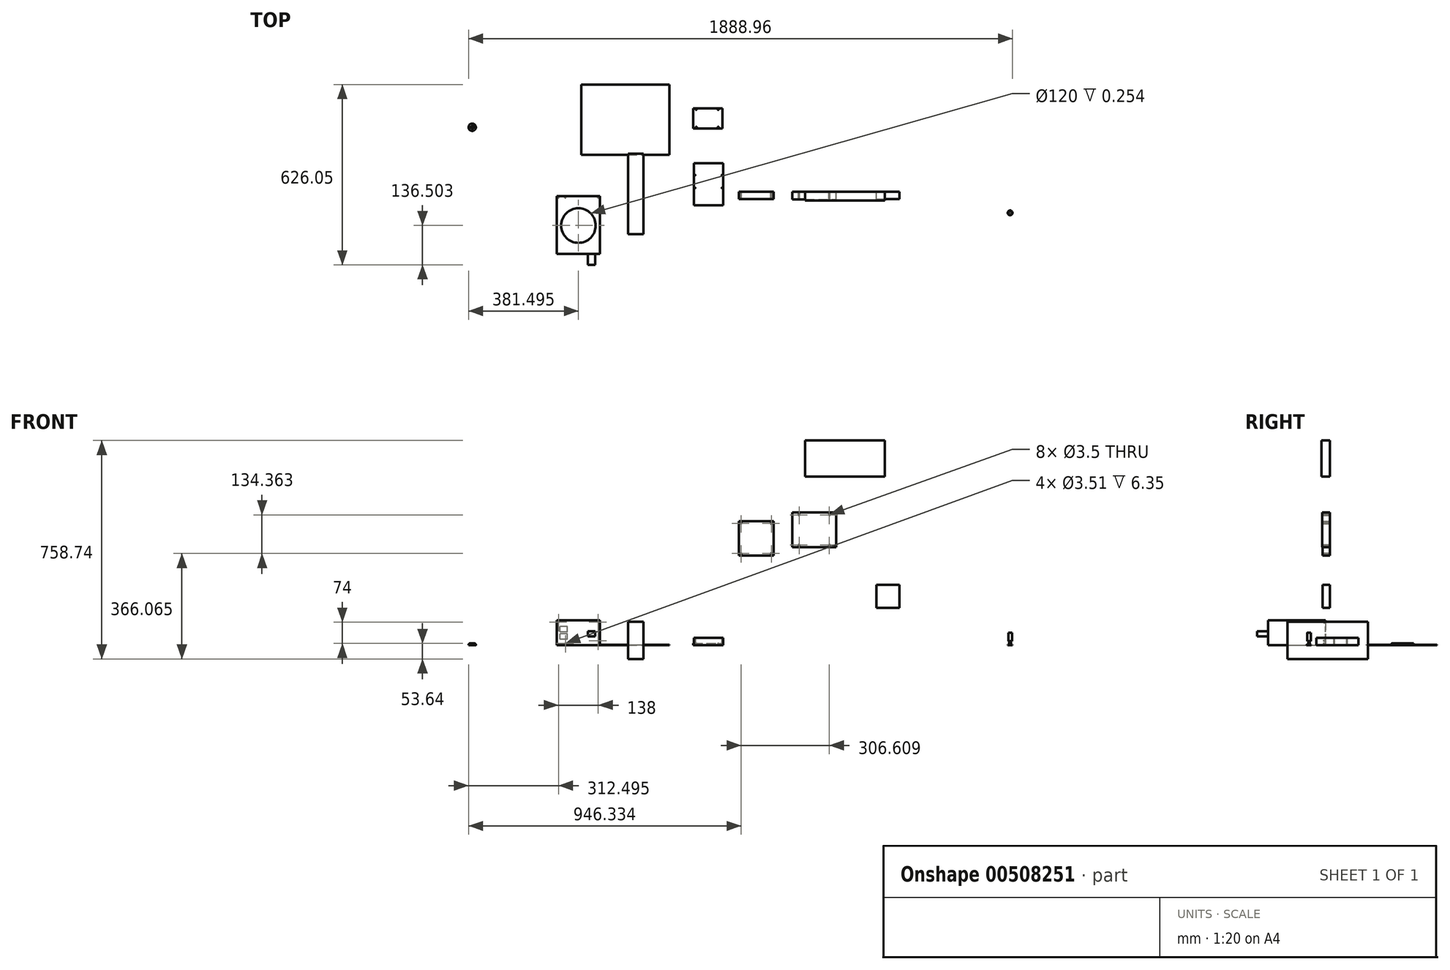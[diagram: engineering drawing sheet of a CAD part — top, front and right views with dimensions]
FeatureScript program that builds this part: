
annotation { "Feature Type Name" : "Feature", "Feature Type Description" : "" }
export const myFeature = defineFeature(function(context is Context, id is Id, definition is map)
    precondition{}
    {
        {
            var Q0;
            Q0=qCreatedBy(makeId("Top.planeOp"),FACE);
            var sketch = newSketch(context, id + "F0", { "sketchPlane" : qUnion([Q0])});
            skLineSegment(sketch, "E0.bottom", {"start": v(-163.1, 128.22) * mm, "end": v(142.9, 128.22) * mm});
            skLineSegment(sketch, "E0.top", {"start": v(-163.1, 372.22) * mm, "end": v(142.9, 372.22) * mm});
            skLineSegment(sketch, "E0.left", {"start": v(-163.1, 128.22) * mm, "end": v(-163.1, 372.22) * mm});
            skLineSegment(sketch, "E0.right", {"start": v(142.9, 128.22) * mm, "end": v(142.9, 372.22) * mm});
            skSolve(sketch);
        }
        {
            var Q0;
            Q0=makeQuery(id+"F0.imprint","IMPRINT",FACE,{"disambiguationData":[TD([[makeQuery(id+"F0.imprint","IMPRINT",EDGE,{"derivedFrom":sQuery(id+"F0.wireOp",EDGE,"E0.bottom")}),1.0]])]});
            extrude(context, id + "F1", {"entities" : qUnion([Q0]), "depth" : 1.6 * mm});
        }
        {
            var Q0;
            Q0=qCreatedBy(makeId("Right.planeOp"),FACE);
            var sketch = newSketch(context, id + "F2", { "sketchPlane" : qUnion([Q0])});
            skLineSegment(sketch, "E1.bottom", {"start": v(-147.7, -47.64) * mm, "end": v(131.7, -47.64) * mm});
            skLineSegment(sketch, "E1.top", {"start": v(-147.7, 81.9) * mm, "end": v(131.7, 81.9) * mm});
            skLineSegment(sketch, "E1.left", {"start": v(-147.7, -47.64) * mm, "end": v(-147.7, 81.9) * mm});
            skLineSegment(sketch, "E1.right", {"start": v(131.7, -47.64) * mm, "end": v(131.7, 81.9) * mm});
            skSolve(sketch);
        }
        {
            var Q0;
            Q0=makeQuery(id+"F2.imprint","IMPRINT",FACE,{"disambiguationData":[TD([[makeQuery(id+"F2.imprint","IMPRINT",EDGE,{"derivedFrom":sQuery(id+"F2.wireOp",EDGE,"E1.bottom")}),1.0]])]});
            extrude(context, id + "F3", {"entities" : qUnion([Q0]), "depth" : 53.34 * mm, "offsetDistance" : 25.4 * mm});
        }
        {
            var Q0;
            Q0=qCreatedBy(makeId("Top.planeOp"),FACE);
            var sketch = newSketch(context, id + "F4", { "sketchPlane" : qUnion([Q0])});
            skLineSegment(sketch, "E2.bottom", {"start": v(-97.62, -215.73) * mm, "end": v(-247.62, -215.73) * mm});
            skLineSegment(sketch, "E2.top", {"start": v(-97.62, -15.73) * mm, "end": v(-247.62, -15.73) * mm});
            skLineSegment(sketch, "E2.left", {"start": v(-97.62, -215.73) * mm, "end": v(-97.62, -15.73) * mm});
            skLineSegment(sketch, "E2.right", {"start": v(-247.62, -215.73) * mm, "end": v(-247.62, -15.73) * mm});
            skSolve(sketch);
        }
        {
            var Q0;
            Q0=makeQuery(id+"F4.imprint","IMPRINT",FACE,{"disambiguationData":[TD([[makeQuery(id+"F4.imprint","IMPRINT",EDGE,{"derivedFrom":sQuery(id+"F4.wireOp",EDGE,"E2.bottom")}),-1.0]])]});
            extrude(context, id + "F5", {"entities" : qUnion([Q0]), "depth" : 86 * mm});
        }
        {
            var Q0;
            Q0=qCreatedBy(makeId("Front.planeOp"),FACE);
            var sketch = newSketch(context, id + "F6", { "sketchPlane" : qUnion([Q0])});
            skLineSegment(sketch, "E3.bottom", {"start": v(384.72, 430.92) * mm, "end": v(504.72, 430.92) * mm});
            skLineSegment(sketch, "E3.top", {"start": v(384.72, 310.92) * mm, "end": v(504.72, 310.92) * mm});
            skLineSegment(sketch, "E3.left", {"start": v(384.72, 430.92) * mm, "end": v(384.72, 310.92) * mm});
            skLineSegment(sketch, "E3.right", {"start": v(504.72, 430.92) * mm, "end": v(504.72, 310.92) * mm});
            skCircle(sketch, "E4", {"center": v(392.22, 423.42) * mm, "radius": 1.75 * mm});
            skCircle(sketch, "E5", {"center": v(497.22, 423.42) * mm, "radius": 1.75 * mm});
            skCircle(sketch, "E6", {"center": v(497.22, 318.42) * mm, "radius": 1.75 * mm});
            skCircle(sketch, "E7", {"center": v(392.22, 318.42) * mm, "radius": 1.75 * mm});
            skLineSegment(sketch, "E8", {"start": v(392.22, 423.42) * mm, "end": v(497.22, 423.42) * mm, "construction": true});
            skLineSegment(sketch, "E9", {"start": v(497.22, 318.42) * mm, "end": v(392.22, 318.42) * mm, "construction": true});
            skLineSegment(sketch, "E10", {"start": v(392.22, 423.42) * mm, "end": v(392.22, 318.42) * mm, "construction": true});
            skLineSegment(sketch, "E11", {"start": v(497.22, 423.42) * mm, "end": v(497.22, 318.42) * mm, "construction": true});
            skLineSegment(sketch, "E12", {"start": v(444.72, 423.42) * mm, "end": v(444.72, 430.92) * mm, "construction": true});
            skLineSegment(sketch, "E13", {"start": v(444.72, 318.42) * mm, "end": v(444.72, 310.92) * mm, "construction": true});
            skSolve(sketch);
        }
        {
            var Q0;
            Q0=makeQuery(id+"F6.imprint","IMPRINT",FACE,{"disambiguationData":[TD([[makeQuery(id+"F6.imprint","IMPRINT",EDGE,{"derivedFrom":sQuery(id+"F6.wireOp",EDGE,"E3.bottom")}),-1.0]])]});
            extrude(context, id + "F7", {"entities" : qUnion([Q0]), "depth" : 25.4 * mm, "offsetDistance" : 25.4 * mm});
        }
        {
            var Q0;
            Q0=qCreatedBy(makeId("Front.planeOp"),FACE);
            var sketch = newSketch(context, id + "F8", { "sketchPlane" : qUnion([Q0])});
            skLineSegment(sketch, "E14.bottom", {"start": v(862.18, 210.36) * mm, "end": v(942.18, 210.36) * mm});
            skLineSegment(sketch, "E14.top", {"start": v(862.18, 130.36) * mm, "end": v(942.18, 130.36) * mm});
            skLineSegment(sketch, "E14.left", {"start": v(862.18, 210.36) * mm, "end": v(862.18, 130.36) * mm});
            skLineSegment(sketch, "E14.right", {"start": v(942.18, 210.36) * mm, "end": v(942.18, 130.36) * mm});
            skSolve(sketch);
        }
        {
            var Q0;
            Q0=makeQuery(id+"F8.imprint","IMPRINT",FACE,{"disambiguationData":[TD([[makeQuery(id+"F8.imprint","IMPRINT",EDGE,{"derivedFrom":sQuery(id+"F8.wireOp",EDGE,"E14.bottom")}),-1.0]])]});
            extrude(context, id + "F9", {"entities" : qUnion([Q0]), "depth" : 25.4 * mm, "offsetDistance" : 25.4 * mm});
        }
        {
            var Q0;
            Q0=qCreatedBy(makeId("Front.planeOp"),FACE);
            var sketch = newSketch(context, id + "F10", { "sketchPlane" : qUnion([Q0])});
            skLineSegment(sketch, "E15.bottom", {"start": v(570.13, 460.61) * mm, "end": v(722.53, 460.61) * mm});
            skLineSegment(sketch, "E15.top", {"start": v(570.13, 339.96) * mm, "end": v(722.53, 339.96) * mm});
            skLineSegment(sketch, "E15.left", {"start": v(570.13, 460.61) * mm, "end": v(570.13, 339.96) * mm});
            skLineSegment(sketch, "E15.right", {"start": v(722.53, 460.61) * mm, "end": v(722.53, 339.96) * mm});
            skCircle(sketch, "E16", {"center": v(593.83, 452.79) * mm, "radius": 1.75 * mm});
            skCircle(sketch, "E17", {"center": v(698.83, 452.79) * mm, "radius": 1.75 * mm});
            skCircle(sketch, "E18", {"center": v(698.83, 347.79) * mm, "radius": 1.75 * mm});
            skCircle(sketch, "E19", {"center": v(593.83, 347.79) * mm, "radius": 1.75 * mm});
            skLineSegment(sketch, "E20", {"start": v(593.83, 452.79) * mm, "end": v(698.83, 452.79) * mm, "construction": true});
            skLineSegment(sketch, "E21", {"start": v(698.83, 347.79) * mm, "end": v(593.83, 347.79) * mm, "construction": true});
            skLineSegment(sketch, "E22", {"start": v(593.83, 452.79) * mm, "end": v(593.83, 347.79) * mm, "construction": true});
            skLineSegment(sketch, "E23", {"start": v(698.83, 452.79) * mm, "end": v(698.83, 347.79) * mm, "construction": true});
            skLineSegment(sketch, "E24", {"start": v(646.33, 347.79) * mm, "end": v(646.33, 340.29) * mm, "construction": true});
            skLineSegment(sketch, "E25", {"start": v(646.33, 460.29) * mm, "end": v(646.33, 452.79) * mm, "construction": true});
            skLineSegment(sketch, "E26", {"start": v(593.83, 400.29) * mm, "end": v(570.13, 400.29) * mm, "construction": true});
            skPoint(sketch, "E26.endSnap0", {"position": v(570.13, 400.29) * mm});
            skLineSegment(sketch, "E27", {"start": v(698.83, 400.29) * mm, "end": v(722.53, 400.29) * mm, "construction": true});
            skSolve(sketch);
        }
        {
            var Q0;
            Q0=makeQuery(id+"F10.imprint","IMPRINT",FACE,{"disambiguationData":[TD([[makeQuery(id+"F10.imprint","IMPRINT",EDGE,{"derivedFrom":sQuery(id+"F10.wireOp",EDGE,"E15.bottom")}),-1.0]])]});
            extrude(context, id + "F11", {"entities" : qUnion([Q0]), "depth" : 27 * mm, "offsetDistance" : 25.4 * mm});
        }
        {
            var Q0;
            Q0=qCreatedBy(makeId("Top.planeOp"),FACE);
            var sketch = newSketch(context, id + "F12", { "sketchPlane" : qUnion([Q0])});
            skLineSegment(sketch, "E28.bottom", {"start": v(228.67, -46.9) * mm, "end": v(330.27, -46.9) * mm});
            skLineSegment(sketch, "E28.top", {"start": v(228.67, 99.15) * mm, "end": v(330.27, 99.15) * mm});
            skLineSegment(sketch, "E28.left", {"start": v(228.67, -46.9) * mm, "end": v(228.67, 99.15) * mm});
            skLineSegment(sketch, "E28.right", {"start": v(330.27, -46.9) * mm, "end": v(330.27, 99.15) * mm});
            skSolve(sketch);
        }
        {
            var Q0;
            Q0=makeQuery(id+"F12.imprint","IMPRINT",FACE,{"disambiguationData":[TD([[makeQuery(id+"F12.imprint","IMPRINT",EDGE,{"derivedFrom":sQuery(id+"F12.wireOp",EDGE,"E28.bottom")}),1.0]])]});
            extrude(context, id + "F13", {"entities" : qUnion([Q0]), "depth" : 25.4 * mm, "offsetDistance" : 25.4 * mm});
        }
        {
            var Q0;
            Q0=qCreatedBy(makeId("Top.planeOp"),FACE);
            var sketch = newSketch(context, id + "F14", { "sketchPlane" : qUnion([Q0])});
            skLineSegment(sketch, "E29.bottom", {"start": v(225.53, 219.96) * mm, "end": v(327.13, 219.96) * mm});
            skLineSegment(sketch, "E29.top", {"start": v(225.53, 289.81) * mm, "end": v(327.13, 289.81) * mm});
            skLineSegment(sketch, "E29.left", {"start": v(225.53, 219.96) * mm, "end": v(225.53, 289.81) * mm});
            skLineSegment(sketch, "E29.right", {"start": v(327.13, 219.96) * mm, "end": v(327.13, 289.81) * mm});
            skSolve(sketch);
        }
        {
            var Q0;
            Q0=makeQuery(id+"F14.imprint","IMPRINT",FACE,{"disambiguationData":[TD([[makeQuery(id+"F14.imprint","IMPRINT",EDGE,{"derivedFrom":sQuery(id+"F14.wireOp",EDGE,"E29.bottom")}),1.0]])]});
            extrude(context, id + "F15", {"entities" : qUnion([Q0]), "depth" : 7 * mm, "offsetDistance" : 25.4 * mm});
        }
        {
            var Q0;
            Q0=makeQuery(id+"F5.opExtrude","SWEPT_FACE",FACE,{"disambiguationData":[OSD([sQuery(id+"F4.wireOp",EDGE,"E2.top")])]});
            var sketch = newSketch(context, id + "F16", { "sketchPlane" : qUnion([Q0])});
            skLineSegment(sketch, "E30.bottom", {"start": v(247.62, 86) * mm, "end": v(247.62, 0) * mm, "construction": true});
            skLineSegment(sketch, "E30.top", {"start": v(97.62, 86) * mm, "end": v(97.62, 0) * mm, "construction": true});
            skLineSegment(sketch, "E30.left", {"start": v(247.62, 86) * mm, "end": v(97.62, 86) * mm, "construction": true});
            skLineSegment(sketch, "E30.right", {"start": v(247.62, 0) * mm, "end": v(97.62, 0) * mm, "construction": true});
            skPoint(sketch, "E31", {"position": v(103.62, 16) * mm});
            skPoint(sketch, "E32", {"position": v(103.62, 80) * mm});
            skPoint(sketch, "E33", {"position": v(241.62, 80) * mm});
            skPoint(sketch, "E34", {"position": v(217.62, 6) * mm});
            skCircle(sketch, "E35", {"center": v(103.62, 80) * mm, "radius": 1.75 * mm});
            skCircle(sketch, "E36", {"center": v(103.62, 16) * mm, "radius": 1.75 * mm});
            skCircle(sketch, "E37", {"center": v(217.62, 6) * mm, "radius": 1.75 * mm});
            skCircle(sketch, "E38", {"center": v(241.62, 80) * mm, "radius": 1.75 * mm});
            skSolve(sketch);
        }
        {
            var Q0;
            Q0 = qSketchRegion(id + "F16", true);
            extrude(context, id + "F17", {"entities" : qUnion([Q0]), "operationType" : NewBodyOperationType.REMOVE, "oppositeDirection" : true, "depth" : 6.35 * mm, "offsetDistance" : 25.4 * mm});
        }
        {
            var Q0;
            Q0=makeQuery(id+"F5.opExtrude","CAP_FACE",FACE,{"disambiguationData":[OSD([sQuery(id+"F4.wireOp",EDGE,"E2.bottom"),sQuery(id+"F4.wireOp",EDGE,"E2.top"),sQuery(id+"F4.wireOp",EDGE,"E2.left"),sQuery(id+"F4.wireOp",EDGE,"E2.right")])],"isStart":false});
            var sketch = newSketch(context, id + "F18", { "sketchPlane" : qUnion([Q0])});
            skCircle(sketch, "E39", {"center": v(-172.62, -117.33) * mm, "radius": 60 * mm});
            skLineSegment(sketch, "E40", {"start": v(-172.62, -117.33) * mm, "end": v(-172.62, -15.73) * mm, "construction": true});
            skSolve(sketch);
        }
        {
            var Q0;
            Q0=makeQuery(id+"F18.imprint","IMPRINT",FACE,{"disambiguationData":[TD([[makeQuery(id+"F18.imprint","IMPRINT",EDGE,{"derivedFrom":sQuery(id+"F18.wireOp",EDGE,"E39")}),1.0]])]});
            extrude(context, id + "F19", {"entities" : qUnion([Q0]), "operationType" : NewBodyOperationType.REMOVE, "oppositeDirection" : true, "depth" : 0.25 * mm, "offsetDistance" : 25.4 * mm});
        }
        {
            var Q0;
            Q0=makeQuery(id+"F5.opExtrude","SWEPT_FACE",FACE,{"disambiguationData":[OSD([sQuery(id+"F4.wireOp",EDGE,"E2.top")])]});
            var sketch = newSketch(context, id + "F20", { "sketchPlane" : qUnion([Q0])});
            skLineSegment(sketch, "E41.bottom", {"start": v(210.42, 20.99) * mm, "end": v(235.82, 20.99) * mm});
            skLineSegment(sketch, "E41.top", {"start": v(210.42, 40.04) * mm, "end": v(235.82, 40.04) * mm});
            skLineSegment(sketch, "E41.left", {"start": v(210.42, 20.99) * mm, "end": v(210.42, 40.04) * mm});
            skLineSegment(sketch, "E41.right", {"start": v(235.82, 20.99) * mm, "end": v(235.82, 40.04) * mm});
            skLineSegment(sketch, "E42.bottom", {"start": v(210.42, 46.39) * mm, "end": v(235.82, 46.39) * mm});
            skLineSegment(sketch, "E42.top", {"start": v(210.42, 65.44) * mm, "end": v(235.82, 65.44) * mm});
            skLineSegment(sketch, "E42.left", {"start": v(210.42, 46.39) * mm, "end": v(210.42, 65.44) * mm});
            skLineSegment(sketch, "E42.right", {"start": v(235.82, 46.39) * mm, "end": v(235.82, 65.44) * mm});
            skLineSegment(sketch, "E43", {"start": v(223.12, 6) * mm, "end": v(217.62, 6) * mm, "construction": true});
            skLineSegment(sketch, "E44", {"start": v(223.12, 6) * mm, "end": v(223.12, 20.99) * mm, "construction": true});
            skSolve(sketch);
        }
        {
            var Q0;
            Q0=makeQuery(id+"F20.imprint","IMPRINT",FACE,{"disambiguationData":[TD([[makeQuery(id+"F20.imprint","IMPRINT",EDGE,{"derivedFrom":sQuery(id+"F20.wireOp",EDGE,"E41.bottom")}),1.0]])]});
            var Q1;
            Q1=makeQuery(id+"F20.imprint","IMPRINT",FACE,{"disambiguationData":[TD([[makeQuery(id+"F20.imprint","IMPRINT",EDGE,{"derivedFrom":sQuery(id+"F20.wireOp",EDGE,"E42.bottom")}),1.0]])]});
            extrude(context, id + "F21", {"entities" : qUnion([Q0, Q1]), "operationType" : NewBodyOperationType.ADD, "depth" : 0.25 * mm, "offsetDistance" : 25.4 * mm});
        }
        {
            var Q0;
            Q0=qCreatedBy(makeId("Top.planeOp"),FACE);
            var sketch = newSketch(context, id + "F22", { "sketchPlane" : qUnion([Q0])});
            skCircle(sketch, "E45", {"center": v(1326.52, -73.23) * mm, "radius": 8.33 * mm});
            skSolve(sketch);
        }
        {
            var Q0;
            Q0=makeQuery(id+"F22.imprint","IMPRINT",FACE,{"disambiguationData":[TD([[makeQuery(id+"F22.imprint","IMPRINT",EDGE,{"derivedFrom":sQuery(id+"F22.wireOp",EDGE,"E45")}),1.0]])]});
            extrude(context, id + "F23", {"entities" : qUnion([Q0]), "depth" : 2.06 * mm, "offsetDistance" : 25.4 * mm});
        }
        {
            var Q0;
            Q0=makeQuery(id+"F23.opExtrude","CAP_FACE",FACE,{"disambiguationData":[OSD([sQuery(id+"F22.wireOp",EDGE,"E45")])],"isStart":false});
            var sketch = newSketch(context, id + "F24", { "sketchPlane" : qUnion([Q0])});
            skCircle(sketch, "E46", {"center": v(1326.52, -73.23) * mm, "radius": 3.97 * mm});
            skSolve(sketch);
        }
        {
            var Q0;
            Q0=makeQuery(id+"F24.imprint","IMPRINT",FACE,{"disambiguationData":[TD([[makeQuery(id+"F24.imprint","IMPRINT",EDGE,{"derivedFrom":sQuery(id+"F24.wireOp",EDGE,"E46")}),1.0]])]});
            extrude(context, id + "F25", {"entities" : qUnion([Q0]), "operationType" : NewBodyOperationType.ADD, "depth" : 3.17 * mm, "offsetDistance" : 25.4 * mm, "hasDraft" : true, "draftAngle" : 20 * degree, "draftPullDirection" : true});
        }
        {
            var Q0;
            Q0=makeQuery(id+"F25.opExtrude","CAP_FACE",FACE,{"disambiguationData":[OSD([sQuery(id+"F24.wireOp",EDGE,"E46")])],"isStart":false});
            var sketch = newSketch(context, id + "F26", { "sketchPlane" : qUnion([Q0])});
            skCircle(sketch, "E47", {"center": v(1326.52, -73.23) * mm, "radius": 2.7 * mm});
            skSolve(sketch);
        }
        {
            var Q0;
            Q0 = qSketchRegion(id + "F26", true);
            extrude(context, id + "F27", {"entities" : qUnion([Q0]), "operationType" : NewBodyOperationType.ADD, "depth" : 38.1 * mm, "offsetDistance" : 25.4 * mm});
        }
        {
            var Q0;
            Q0=makeQuery(id+"F13.opExtrude","CAP_FACE",FACE,{"disambiguationData":[OSD([sQuery(id+"F12.wireOp",EDGE,"E28.bottom"),sQuery(id+"F12.wireOp",EDGE,"E28.top"),sQuery(id+"F12.wireOp",EDGE,"E28.left"),sQuery(id+"F12.wireOp",EDGE,"E28.right")])],"isStart":true});
            var sketch = newSketch(context, id + "F28", { "sketchPlane" : qUnion([Q0])});
            skLineSegment(sketch, "E48.bottom", {"start": v(228.67, 46.9) * mm, "end": v(330.27, 46.9) * mm, "construction": true});
            skLineSegment(sketch, "E48.top", {"start": v(228.67, -99.15) * mm, "end": v(330.27, -99.15) * mm, "construction": true});
            skLineSegment(sketch, "E48.left", {"start": v(228.67, 46.9) * mm, "end": v(228.67, -99.15) * mm, "construction": true});
            skLineSegment(sketch, "E48.right", {"start": v(330.27, 46.9) * mm, "end": v(330.27, -99.15) * mm, "construction": true});
            skCircle(sketch, "E49", {"center": v(231.85, -13.42) * mm, "radius": 1.59 * mm});
            skCircle(sketch, "E50", {"center": v(327.1, -13.42) * mm, "radius": 1.59 * mm});
            skCircle(sketch, "E51", {"center": v(231.85, -57.87) * mm, "radius": 1.59 * mm});
            skCircle(sketch, "E52", {"center": v(327.1, -57.87) * mm, "radius": 1.59 * mm});
            skLineSegment(sketch, "E53", {"start": v(231.85, -13.42) * mm, "end": v(327.1, -13.42) * mm, "construction": true});
            skLineSegment(sketch, "E54", {"start": v(327.1, -13.42) * mm, "end": v(327.1, -57.87) * mm, "construction": true});
            skLineSegment(sketch, "E55", {"start": v(327.1, -57.87) * mm, "end": v(231.85, -57.87) * mm, "construction": true});
            skLineSegment(sketch, "E56", {"start": v(231.85, -13.42) * mm, "end": v(231.85, -57.87) * mm, "construction": true});
            skLineSegment(sketch, "E57.bottom", {"start": v(225.53, -219.96) * mm, "end": v(327.13, -219.96) * mm, "construction": true});
            skLineSegment(sketch, "E57.top", {"start": v(225.53, -289.81) * mm, "end": v(327.13, -289.81) * mm, "construction": true});
            skLineSegment(sketch, "E57.left", {"start": v(225.53, -219.96) * mm, "end": v(225.53, -289.81) * mm, "construction": true});
            skLineSegment(sketch, "E57.right", {"start": v(327.13, -219.96) * mm, "end": v(327.13, -289.81) * mm, "construction": true});
            skCircle(sketch, "E58", {"center": v(313.13, -224.04) * mm, "radius": 1.59 * mm});
            skCircle(sketch, "E59", {"center": v(313.13, -285.75) * mm, "radius": 1.59 * mm});
            skCircle(sketch, "E60", {"center": v(236.53, -224.04) * mm, "radius": 1.59 * mm});
            skCircle(sketch, "E61", {"center": v(236.53, -285.75) * mm, "radius": 1.59 * mm});
            skLineSegment(sketch, "E62", {"start": v(236.53, -224.04) * mm, "end": v(313.13, -224.04) * mm, "construction": true});
            skLineSegment(sketch, "E63", {"start": v(313.13, -224.04) * mm, "end": v(313.13, -285.75) * mm, "construction": true});
            skLineSegment(sketch, "E64", {"start": v(313.13, -285.75) * mm, "end": v(236.53, -285.75) * mm, "construction": true});
            skLineSegment(sketch, "E65", {"start": v(236.53, -285.75) * mm, "end": v(236.53, -224.04) * mm, "construction": true});
            skSolve(sketch);
        }
        {
            var Q0;
            Q0 = qSketchRegion(id + "F28", true);
            extrude(context, id + "F29", {"entities" : qUnion([Q0]), "operationType" : NewBodyOperationType.REMOVE, "endBound" : BoundingType.THROUGH_ALL, "oppositeDirection" : true, "depth" : 25.4 * mm, "offsetDistance" : 25.4 * mm});
        }
        {
            var Q0;
            Q0=qCreatedBy(makeId("Top.planeOp"),FACE);
            var sketch = newSketch(context, id + "F30", { "sketchPlane" : qUnion([Q0])});
            skCircle(sketch, "E66", {"center": v(-541.4, 223.97) * mm, "radius": 12.7 * mm});
            skSolve(sketch);
        }
        {
            var Q0;
            Q0=makeQuery(id+"F30.imprint","IMPRINT",FACE,{"disambiguationData":[TD([[makeQuery(id+"F30.imprint","IMPRINT",EDGE,{"derivedFrom":sQuery(id+"F30.wireOp",EDGE,"E66")}),1.0]])]});
            extrude(context, id + "F31", {"entities" : qUnion([Q0]), "depth" : 6.35 * mm, "offsetDistance" : 25.4 * mm});
        }
        {
            var Q0;
            Q0=makeQuery(id+"F31.opExtrude","CAP_FACE",FACE,{"disambiguationData":[OSD([sQuery(id+"F30.wireOp",EDGE,"E66")])],"isStart":false});
            var sketch = newSketch(context, id + "F32", { "sketchPlane" : qUnion([Q0])});
            skCircle(sketch, "E67", {"center": v(-541.4, 223.97) * mm, "radius": 4.76 * mm});
            skSolve(sketch);
        }
        {
            var Q0;
            Q0=makeQuery(id+"F32.imprint","IMPRINT",FACE,{"disambiguationData":[TD([[makeQuery(id+"F32.imprint","IMPRINT",EDGE,{"derivedFrom":sQuery(id+"F32.wireOp",EDGE,"E67")}),1.0]])]});
            extrude(context, id + "F33", {"entities" : qUnion([Q0]), "operationType" : NewBodyOperationType.REMOVE, "oppositeDirection" : true, "depth" : 3.17 * mm, "offsetDistance" : 25.4 * mm});
        }
        {
            var Q0;
            Q0=makeQuery(id+"F31.opExtrude","CAP_EDGE",EDGE,{"disambiguationData":[OSD([sQuery(id+"F30.wireOp",EDGE,"E66")])],"isStart":false});
            fillet(context, id + "F34", {"entities" : qUnion([Q0]), "radius" : 5.08 * mm, "tangentPropagation" : true, "allowEdgeOverflow" : false});
        }
        {
            var Q0;
            Q0=makeQuery(id+"F5.opExtrude","SWEPT_FACE",FACE,{"disambiguationData":[OSD([sQuery(id+"F4.wireOp",EDGE,"E2.bottom")])]});
            var sketch = newSketch(context, id + "F35", { "sketchPlane" : qUnion([Q0])});
            skLineSegment(sketch, "E68.bottom", {"start": v(-140.12, 30.63) * mm, "end": v(-113.9, 30.63) * mm});
            skLineSegment(sketch, "E68.top", {"start": v(-140.12, 48.4) * mm, "end": v(-113.9, 48.4) * mm});
            skLineSegment(sketch, "E68.left", {"start": v(-140.12, 30.63) * mm, "end": v(-140.12, 48.4) * mm});
            skLineSegment(sketch, "E68.right", {"start": v(-113.9, 30.63) * mm, "end": v(-113.9, 48.4) * mm});
            skSolve(sketch);
        }
        {
            var Q0;
            Q0=makeQuery(id+"F35.imprint","IMPRINT",FACE,{"disambiguationData":[TD([[makeQuery(id+"F35.imprint","IMPRINT",EDGE,{"derivedFrom":sQuery(id+"F35.wireOp",EDGE,"E68.bottom")}),1.0]])]});
            extrude(context, id + "F36", {"entities" : qUnion([Q0]), "operationType" : NewBodyOperationType.ADD, "depth" : 38.1 * mm, "offsetDistance" : 25.4 * mm});
        }
        {
            var Q0;
            Q0=qCreatedBy(makeId("Front.planeOp"),FACE);
            var sketch = newSketch(context, id + "F37", { "sketchPlane" : qUnion([Q0])});
            skLineSegment(sketch, "E69.bottom", {"start": v(615.1, 711.1) * mm, "end": v(891.1, 711.1) * mm});
            skLineSegment(sketch, "E69.top", {"start": v(615.1, 586.1) * mm, "end": v(891.1, 586.1) * mm});
            skLineSegment(sketch, "E69.left", {"start": v(615.1, 711.1) * mm, "end": v(615.1, 586.1) * mm});
            skLineSegment(sketch, "E69.right", {"start": v(891.1, 711.1) * mm, "end": v(891.1, 586.1) * mm});
            skSolve(sketch);
        }
        {
            var Q0;
            Q0=makeQuery(id+"F37.imprint","IMPRINT",FACE,{"disambiguationData":[TD([[makeQuery(id+"F37.imprint","IMPRINT",EDGE,{"derivedFrom":sQuery(id+"F37.wireOp",EDGE,"E69.bottom")}),-1.0]])]});
            extrude(context, id + "F38", {"entities" : qUnion([Q0]), "depth" : 30 * mm, "offsetDistance" : 25.4 * mm});
        }
        {
            var Q0;
            Q0=makeQuery(id+"F27.opExtrude","CAP_FACE",FACE,{"disambiguationData":[OSD([sQuery(id+"F26.wireOp",EDGE,"E47")])],"isStart":false});
            var sketch = newSketch(context, id + "F39", { "sketchPlane" : qUnion([Q0])});
            skCircle(sketch, "E70", {"center": v(1326.52, -73.23) * mm, "radius": 6.35 * mm});
            skSolve(sketch);
        }
        {
            var Q0;
            Q0=makeQuery(id+"F39.imprint","IMPRINT",FACE,{"disambiguationData":[TD([[makeQuery(id+"F39.imprint","IMPRINT",EDGE,{"derivedFrom":sQuery(id+"F39.wireOp",EDGE,"E70")}),1.0]])]});
            extrude(context, id + "F40", {"entities" : qUnion([Q0]), "operationType" : NewBodyOperationType.ADD, "oppositeDirection" : true, "depth" : 28.57 * mm, "offsetDistance" : 25.4 * mm});
        }
    });
